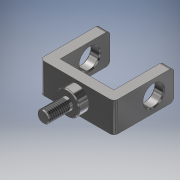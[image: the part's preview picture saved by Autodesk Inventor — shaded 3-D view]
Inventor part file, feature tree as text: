
AUTODESK INVENTOR PART (.ipt)
format: ipt  version: 2018 (Build 220112000, 112)  size: 171,520 bytes
history: native  units: mm
features: extrude x4, sketch x4, other x2, fillet x1, chamfer x1, thread x1
ambient origin geometry x8: Origin, YZ Plane, XZ Plane, XY Plane, X Axis, Y Axis, Z Axis, Center Point
bodies: Solido1 (feature_tree)
feature tree (13):
  extrude  "Estrusione1"  Depth=37.0mm
  extrude  "Estrusione2"  Depth=27.0mm
  fillet  "Raccordo1"  Radius=5.0mm
  extrude  "Estrusione3"  Depth=30.0mm
  extrude  "Estrusione4"  Depth=15.0mm TaperAngle=0.0deg
  chamfer  "Smusso1"  Distance=10.0mm
  thread  "Filettatura2"
  sketch  "Schizzo1"
  sketch  "Schizzo2"
  other  "Linea chiusa proiettata1"
  sketch  "Schizzo3"
  other  "Linea chiusa proiettata2"
  sketch  "Schizzo4"
